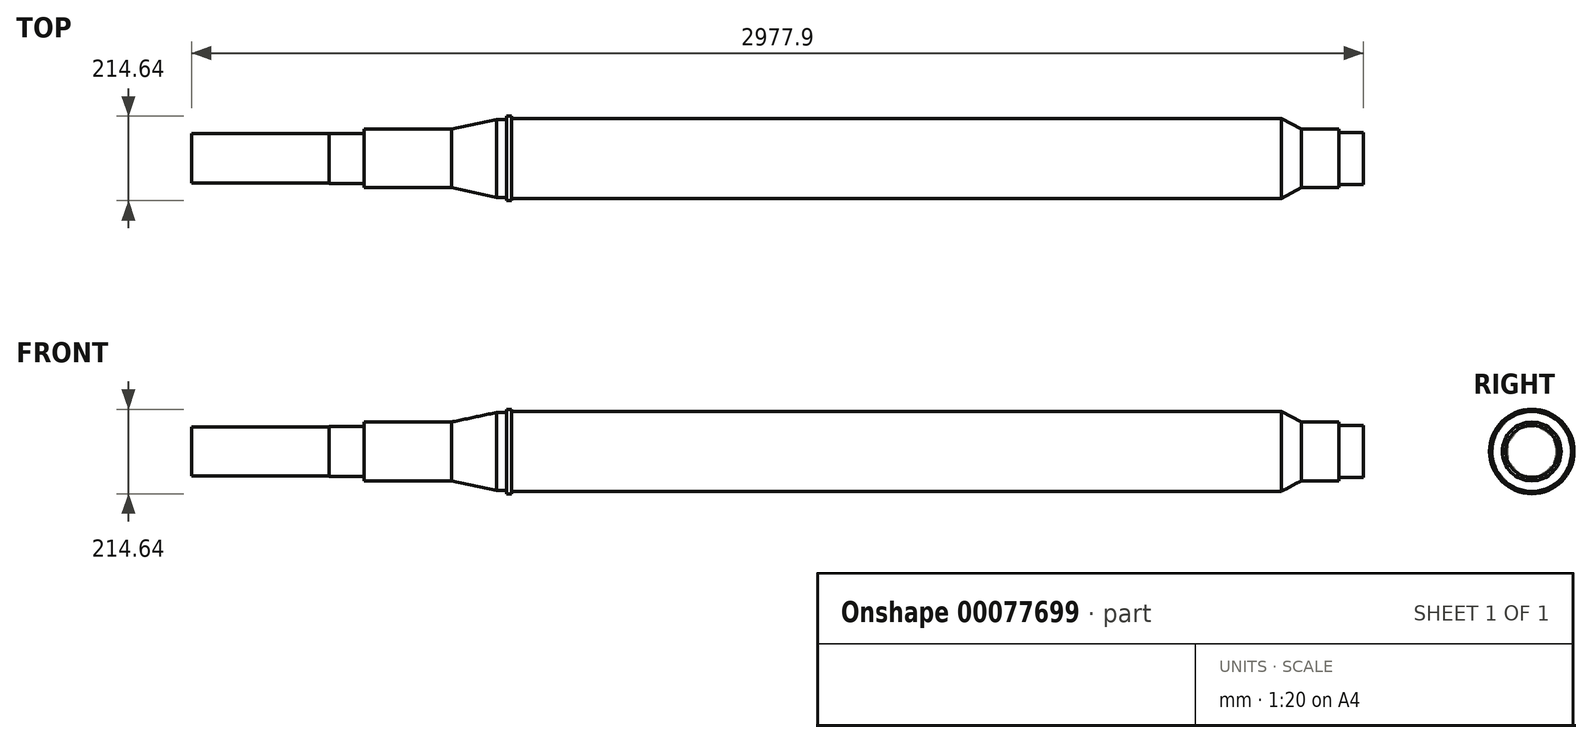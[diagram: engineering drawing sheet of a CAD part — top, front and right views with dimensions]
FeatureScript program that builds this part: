
annotation { "Feature Type Name" : "Feature", "Feature Type Description" : "" }
export const myFeature = defineFeature(function(context is Context, id is Id, definition is map)
    precondition{}
    {
        {
            var Q0;
            Q0=qCreatedBy(makeId("Right.planeOp"),FACE);
            var sketch = newSketch(context, id + "F0", { "sketchPlane" : qUnion([Q0])});
            skCircle(sketch, "E0", {"center": v(0, 0) * mm, "radius": 101.6 * mm});
            skSolve(sketch);
        }
        {
            var Q0;
            Q0=qSketchRegion(id+"F0",true);
            extrude(context, id + "F1", {"entities" : qUnion([Q0]), "endBound" : BoundingType.SYMMETRIC, "depth" : 1955.8 * mm});
        }
        {
            var Q0;
            Q0=makeQuery(id+"F1.opExtrude","CAP_FACE",FACE,{"disambiguationData":[OSD([sQuery(id+"F0.wireOp",EDGE,"E0")])],"isStart":false});
            cPlane(context, id + "F2", {"entities" : qUnion([Q0]), "cplaneType" : CPlaneType.OFFSET, "offset" : 0 * mm, "width" : 152.4 * mm, "height" : 152.4 * mm});
        }
        {
            var Q0;
            Q0=makeQuery(id+"F1.opExtrude","CAP_FACE",FACE,{"disambiguationData":[OSD([sQuery(id+"F0.wireOp",EDGE,"E0")])],"isStart":false});
            cPlane(context, id + "F3", {"entities" : qUnion([Q0]), "cplaneType" : CPlaneType.OFFSET, "offset" : 50.8 * mm, "width" : 152.4 * mm, "height" : 152.4 * mm});
        }
        {
            var Q0;
            Q0=qCreatedBy(id+"F2.planeOp",FACE);
            var sketch = newSketch(context, id + "F4", { "sketchPlane" : qUnion([Q0])});
            skCircle(sketch, "E1.0", {"center": v(0, 0) * mm, "radius": 101.6 * mm});
            skSolve(sketch);
        }
        {
            var Q0;
            Q0=qCreatedBy(id+"F3.planeOp",FACE);
            var sketch = newSketch(context, id + "F5", { "sketchPlane" : qUnion([Q0])});
            skCircle(sketch, "E2", {"center": v(0, 0) * mm, "radius": 74.61 * mm});
            skSolve(sketch);
        }
        {
            var Q1;
            Q1=makeQuery(id+"F4.imprint","IMPRINT",FACE,{"disambiguationData":[TD([[makeQuery(id+"F4.imprint","IMPRINT",EDGE,{"derivedFrom":sQuery(id+"F4.wireOp",EDGE,"E1.0")}),1.0]])]});
            var Q2;
            Q2=makeQuery(id+"F5.imprint","IMPRINT",FACE,{"disambiguationData":[TD([[makeQuery(id+"F5.imprint","IMPRINT",EDGE,{"derivedFrom":sQuery(id+"F5.wireOp",EDGE,"E2")}),1.0]])]});
            loft(context, id + "F6", {"operationType" : NewBodyOperationType.ADD, "sheetProfilesArray" : [{ "sheetProfileEntities" : qUnion([Q1]) }, { "sheetProfileEntities" : qUnion([Q2]) }]});
        }
        {
            var Q0;
            Q0=makeQuery(id+"F6.opLoft","CAP_FACE",FACE,{"disambiguationData":[OSD([makeQuery(id+"F5.imprint","IMPRINT",FACE,{"disambiguationData":[TD([[makeQuery(id+"F5.imprint","IMPRINT",EDGE,{"derivedFrom":sQuery(id+"F5.wireOp",EDGE,"E2")}),1.0]])]})])],"isStart":true});
            extrude(context, id + "F7", {"entities" : qUnion([Q0]), "operationType" : NewBodyOperationType.ADD, "depth" : 95.25 * mm});
        }
        {
            var Q0;
            Q0=makeQuery(id+"F7.opExtrude","CAP_FACE",FACE,{"disambiguationData":[OSD([makeQuery(id+"F5.imprint","IMPRINT",FACE,{"disambiguationData":[TD([[makeQuery(id+"F5.imprint","IMPRINT",EDGE,{"derivedFrom":sQuery(id+"F5.wireOp",EDGE,"E2")}),1.0]])]})])],"isStart":false});
            var sketch = newSketch(context, id + "F8", { "sketchPlane" : qUnion([Q0])});
            skCircle(sketch, "E3", {"center": v(0, 0) * mm, "radius": 66.04 * mm});
            skSolve(sketch);
        }
        {
            var Q0;
            Q0=qSketchRegion(id+"F8",true);
            extrude(context, id + "F9", {"entities" : qUnion([Q0]), "operationType" : NewBodyOperationType.ADD, "depth" : 63.25 * mm});
        }
        {
            var Q0;
            Q0=makeQuery(id+"F1.opExtrude","CAP_FACE",FACE,{"disambiguationData":[OSD([sQuery(id+"F0.wireOp",EDGE,"E0")])],"isStart":true});
            var sketch = newSketch(context, id + "F10", { "sketchPlane" : qUnion([Q0])});
            skCircle(sketch, "E4", {"center": v(0, 0) * mm, "radius": 107.32 * mm});
            skSolve(sketch);
        }
        {
            var Q0;
            Q0=qSketchRegion(id+"F10",true);
            extrude(context, id + "F11", {"entities" : qUnion([Q0]), "operationType" : NewBodyOperationType.ADD, "depth" : 12.7 * mm});
        }
        {
            var Q0;
            Q0=makeQuery(id+"F11.opExtrude","CAP_FACE",FACE,{"disambiguationData":[OSD([sQuery(id+"F10.wireOp",EDGE,"E4")])],"isStart":false});
            var sketch = newSketch(context, id + "F12", { "sketchPlane" : qUnion([Q0])});
            skCircle(sketch, "E5", {"center": v(0, 0) * mm, "radius": 99.19 * mm});
            skSolve(sketch);
        }
        {
            var Q0;
            Q0=qSketchRegion(id+"F12",true);
            extrude(context, id + "F13", {"entities" : qUnion([Q0]), "operationType" : NewBodyOperationType.ADD, "depth" : 25.4 * mm});
        }
        {
            var Q0;
            Q0=makeQuery(id+"F13.opExtrude","CAP_FACE",FACE,{"disambiguationData":[OSD([sQuery(id+"F12.wireOp",EDGE,"E5")])],"isStart":false});
            cPlane(context, id + "F14", {"entities" : qUnion([Q0]), "cplaneType" : CPlaneType.OFFSET, "offset" : 114.3 * mm, "width" : 152.4 * mm, "height" : 152.4 * mm});
        }
        {
            var Q0;
            Q0=qCreatedBy(id+"F14.planeOp",FACE);
            var sketch = newSketch(context, id + "F15", { "sketchPlane" : qUnion([Q0])});
            skCircle(sketch, "E6", {"center": v(0, 0) * mm, "radius": 74.61 * mm});
            skSolve(sketch);
        }
        {
            var Q1;
            Q1=makeQuery(id+"F13.opExtrude","CAP_FACE",FACE,{"disambiguationData":[OSD([sQuery(id+"F12.wireOp",EDGE,"E5")])],"isStart":false});
            var Q2;
            Q2=makeQuery(id+"F15.imprint","IMPRINT",FACE,{"disambiguationData":[TD([[makeQuery(id+"F15.imprint","IMPRINT",EDGE,{"derivedFrom":sQuery(id+"F15.wireOp",EDGE,"E6")}),1.0]])]});
            loft(context, id + "F16", {"operationType" : NewBodyOperationType.ADD, "sheetProfilesArray" : [{ "sheetProfileEntities" : qUnion([Q1]) }, { "sheetProfileEntities" : qUnion([Q2]) }]});
        }
        {
            var Q0;
            Q0=makeQuery(id+"F16.opLoft","CAP_FACE",FACE,{"disambiguationData":[OSD([makeQuery(id+"F15.imprint","IMPRINT",FACE,{"disambiguationData":[TD([[makeQuery(id+"F15.imprint","IMPRINT",EDGE,{"derivedFrom":sQuery(id+"F15.wireOp",EDGE,"E6")}),1.0]])]})])],"isStart":true});
            extrude(context, id + "F17", {"entities" : qUnion([Q0]), "operationType" : NewBodyOperationType.ADD, "depth" : 222.25 * mm});
        }
        {
            var Q0;
            Q0=makeQuery(id+"F17.opExtrude","CAP_FACE",FACE,{"disambiguationData":[OSD([makeQuery(id+"F15.imprint","IMPRINT",FACE,{"disambiguationData":[TD([[makeQuery(id+"F15.imprint","IMPRINT",EDGE,{"derivedFrom":sQuery(id+"F15.wireOp",EDGE,"E6")}),1.0]])]})])],"isStart":false});
            var sketch = newSketch(context, id + "F18", { "sketchPlane" : qUnion([Q0])});
            skCircle(sketch, "E7", {"center": v(0, 0) * mm, "radius": 63.5 * mm});
            skSolve(sketch);
        }
        {
            var Q0;
            Q0=qSketchRegion(id+"F18",true);
            extrude(context, id + "F19", {"entities" : qUnion([Q0]), "operationType" : NewBodyOperationType.ADD, "depth" : 88.9 * mm});
        }
        {
            var Q0;
            Q0=makeQuery(id+"F19.opExtrude","CAP_FACE",FACE,{"disambiguationData":[OSD([sQuery(id+"F18.wireOp",EDGE,"E7")])],"isStart":false});
            var sketch = newSketch(context, id + "F20", { "sketchPlane" : qUnion([Q0])});
            skCircle(sketch, "E8", {"center": v(0, 0) * mm, "radius": 62.61 * mm});
            skSolve(sketch);
        }
        {
            var Q0;
            Q0=qSketchRegion(id+"F20",true);
            extrude(context, id + "F21", {"entities" : qUnion([Q0]), "operationType" : NewBodyOperationType.ADD, "depth" : 349.25 * mm});
        }
    });
